# Revit family: Lighting_Fixture-Wall-Astro-Monzaxxx
name_source: partatom
category: Lighting Fixtures
revit_build: Autodesk Revit LT 2014 (Build: 20130308_1515(x64)
units: mm (PartAtom-declared; Revit-internal decimal feet)

## types (3) — shared parameters
900 Diffuser Height = 870 mm  [stored 2.85433 ft]
Assembly Code = D5020200
Casing Material = Astro - Steel - Chrome Finish
Class = 2
Color Filter = 16777215
Description = Mirror Light
Dimmable = No
Dimming Lamp Color Temperature Shift = <None>
Emit Shape Visible in Rendering = No
IP Rating = IP44
Lamp included = No
Manufacturer = Astro Lighting Ltd, CM20 2DP
Mountable on normally flammable surfaces = Yes
Number of Poles = 1
Product Documentation = http://www.astrolighting.co.uk
Suitable for bathroom zone = Zones 2 and 3
Tilt Angle = 90.00°
URL = www.astrolighting.co.uk
Voltage = 230 V

## per-type parameters (varying)
| type | 600 Diffuser Height | 600 Diffuser Visibility | 900 Diffuser Visibility | Angle 1 | Angle 2 | Apparent Load | Cable Entry Placement | Emit from Rectangle Length | Emit from Rectangle Width | Height | Lamp | Length | Light Source From Wall | Luminaire Lamp Efficiency Rating | Model | Photometric Web File | Radius Lower Plate | Radius Upper Plate | Type Comments | Wattage Comments | Weight | Width | Width Lower Plate |
| 7017 Monza 600 | 570 mm  [stored 1.87008 ft] | Yes | No | 7.00° | 14.00° | 20 VA | 530 mm  [stored 1.73885 ft] | 116 mm  [stored 0.380577 ft] | 570 mm  [stored 1.87008 ft] | 600 mm | T5 | 88.5 mm  [stored 0.290354 ft] | 44.25 mm  [stored 0.145177 ft] | A-C | 7017 Monza 600 | 7017 MONZA 600.ies | 58 mm  [stored 0.190289 ft] | 62.5 mm  [stored 0.205052 ft] | Includes integral electronic ballast. Can be mounted horizontally or vertically. | 24w | 1.8kg | 125 mm  [stored 0.410105 ft] | 116 mm  [stored 0.380577 ft] |
| 7018 Monza 900 | 570 mm  [stored 1.87008 ft] | No | Yes | 9.25° | 18.50° | 42 VA | 90 mm  [stored 0.295276 ft] | 90 mm  [stored 0.295276 ft] | 870 mm  [stored 2.85433 ft] | 900 mm  [stored 2.95276 ft] | T5 | 74.5 mm  [stored 0.244423 ft] | 37.25 mm  [stored 0.122211 ft] | A-C | 7018 Monza 900 | 7018 MONZA 900.ies | 45 mm  [stored 0.147638 ft] | 50 mm  [stored 0.164042 ft] | Includes integral electronic ballast. Can be mounted horizontally or vertically | 39w | 2.6kg | 100 mm  [stored 0.328084 ft] | 90 mm  [stored 0.295276 ft] |
| 0915 Monza Plus 400 | 370 mm  [stored 1.21391 ft] | Yes | No | 7.00° | 14.00° | 20 VA | 340 mm  [stored 1.11549 ft] | 115 mm  [stored 0.377297 ft] | 370 mm  [stored 1.21391 ft] | 400 mm  [stored 1.31234 ft] | 2G11 | 88.5 mm  [stored 0.290354 ft] | 44.25 mm  [stored 0.145177 ft] | B | 0915 Monza 400 | 0915 monza plus 400.ies | 57.5 mm  [stored 0.188648 ft] | 62.5 mm  [stored 0.205052 ft] | Includes integral electronic ballast. Can be mounted horizontally or vertically. | 24w | 2.62kg | 125 mm  [stored 0.410105 ft] | 115 mm  [stored 0.377297 ft] |

note: [stored X ft] marks values corroborated as IEEE doubles in the binary element streams (Revit-internal decimal feet)

## geometry (parser evidence)
native form markers: Blend x2, Sweep x1
no freeform markers — native parametric forms only
